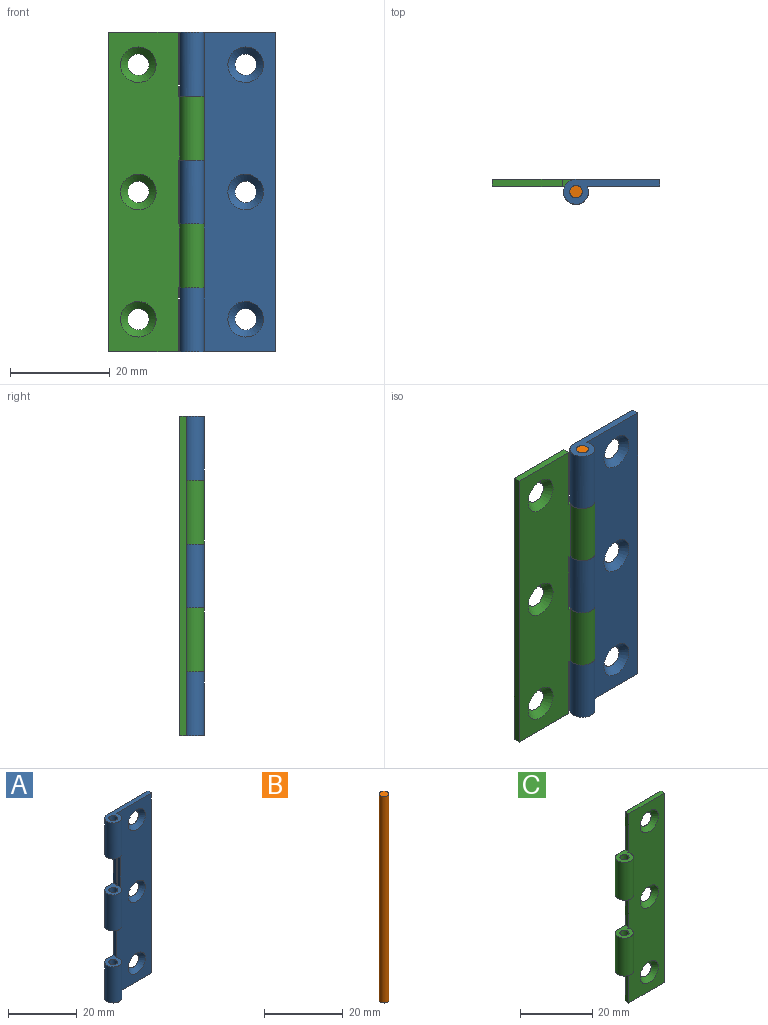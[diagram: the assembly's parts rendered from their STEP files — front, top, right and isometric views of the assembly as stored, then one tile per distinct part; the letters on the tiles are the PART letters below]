
ASSEMBLY  parts=3 mates=2
PART A: 20 faces, bbox 19.2x5x64 mm
  f0: cylinder r=2.5mm len=38.4mm, axis (0,0,-1), area 343.6mm2, adj f2,f5,f7,f12,f15,f16,f17
  f1: cylinder r=2.5mm len=12.8mm, axis (0,0,-1), area 165.4mm2, adj f2,f5,f8,f13
  f2: plane 64x14.5mm, normal (0,-1,0), area 803.3mm2, adj f0,f1,f6,f7,f8,f9,f10,f11
  f3: cylinder r=1.25mm len=12.8mm, axis (0,0,-1), area 100.5mm2, adj f7,f15
  f4: cylinder r=1.25mm len=12.8mm, axis (0,0,-1), area 100.5mm2, adj f8,f13
  f5: plane 64x16.75mm, normal (0,1,0), area 964.8mm2, adj f0,f1,f6,f7,f8,f9,f10,f11
  f6: plane 64x1.4mm, normal (1,0,0), area 89.6mm2, adj f2,f5,f7,f8
  f7: plane 19.25x5mm, normal (0,0,1), area 35.9mm2, adj f0,f2,f3,f5,f6
  f8: plane 19.25x5mm, normal (0,0,-1), area 35.9mm2, adj f1,f2,f4,f5,f6
  f9: cone r=2.15mm half-angle=45deg, axis (0,-1,0), area 35.5mm2, adj f2,f5
  f10: cone r=2.15mm half-angle=45deg, axis (0,-1,0), area 35.5mm2, adj f2,f5
  f11: cone r=2.15mm half-angle=45deg, axis (0,-1,0), area 35.5mm2, adj f2,f5
  f12: plane 5x5mm, normal (0,0,-1), area 16mm2, adj f0,f2,f5,f14,f19
  f13: plane 5x5mm, normal (0,0,1), area 16mm2, adj f1,f2,f4,f5,f14
  f14: plane 12.8x1.4mm, normal (-1,0,0), area 17.9mm2, adj f2,f5,f12,f13
  f15: plane 5x4.95mm, normal (0,0,-1), area 15.9mm2, adj f0,f2,f3,f5,f17,f18
  f16: plane 5x4.95mm, normal (0,0,1), area 15.9mm2, adj f0,f2,f5,f17,f18,f19
  f17: plane 12.8x1mm, normal (-1,0,0), area 12.8mm2, adj f0,f15,f16
  f18: plane 12.8x1.4mm, normal (-1,0,0), area 17.9mm2, adj f2,f5,f15,f16
  f19: cylinder r=1.25mm len=12.8mm, axis (0,0,-1), area 100.5mm2, adj f12,f16
PART B: 3 faces, bbox 2.5x2.5x64 mm
  f0: cylinder r=1.25mm len=64mm, axis (0,0,-1), area 502.7mm2, adj f1,f2
  f1: plane 2.5x2.5mm, normal (0,0,1), area 4.9mm2, adj f0
  f2: plane 2.5x2.5mm, normal (0,0,-1), area 4.9mm2, adj f0
PART C: 19 faces, bbox 19.2x5x64 mm
  f0: cylinder r=2.5mm len=12.8mm, axis (0,0,-1), area 165.4mm2, adj f2,f3,f14,f15
  f1: cylinder r=2.5mm len=12.8mm, axis (0,0,-1), area 165.4mm2, adj f2,f3,f10,f12
  f2: plane 64x14.5mm, normal (0,-1,0), area 789.7mm2, adj f0,f1,f4,f5,f6,f7,f8,f9
  f3: plane 64x16.75mm, normal (0,1,0), area 922.4mm2, adj f0,f1,f4,f5,f6,f7,f8,f9
  f4: plane 13.99x1.4mm, normal (0,0,1), area 19.6mm2, adj f2,f3,f6,f16
  f5: plane 13.99x1.4mm, normal (0,0,-1), area 19.6mm2, adj f2,f3,f6,f11
  f6: plane 64x1.4mm, normal (1,0,0), area 89.6mm2, adj f2,f3,f4,f5
  f7: cone r=2.15mm half-angle=45deg, axis (0,-1,0), area 35.5mm2, adj f2,f3
  f8: cone r=2.15mm half-angle=45deg, axis (0,-1,0), area 35.5mm2, adj f2,f3
  f9: cone r=2.15mm half-angle=45deg, axis (0,-1,0), area 35.5mm2, adj f2,f3
  f10: plane 5.25x5mm, normal (0,0,-1), area 16.3mm2, adj f1,f2,f3,f11,f17
  f11: plane 12.8x1.4mm, normal (-1,0,0), area 17.9mm2, adj f2,f3,f5,f10
  f12: plane 5.25x5mm, normal (0,0,1), area 16.3mm2, adj f1,f2,f3,f13,f17
  f13: plane 12.8x1.4mm, normal (-1,0,0), area 17.9mm2, adj f2,f3,f12,f14
  f14: plane 5.25x5mm, normal (0,0,-1), area 16.3mm2, adj f0,f2,f3,f13,f18
  f15: plane 5.25x5mm, normal (0,0,1), area 16.3mm2, adj f0,f2,f3,f16,f18
  f16: plane 12.8x1.4mm, normal (-1,0,0), area 17.9mm2, adj f2,f3,f4,f15
  f17: cylinder r=1.25mm len=12.8mm, axis (0,0,-1), area 100.5mm2, adj f10,f12
  f18: cylinder r=1.25mm len=12.8mm, axis (0,0,-1), area 100.5mm2, adj f14,f15
PLACE A rot(axis=(0,0,1),0deg) t=(0,0,0)mm
PLACE B at identity
PLACE C rot(axis=(0,-1,0),180deg) t=(0,0,64)mm
MATE revolute A.f0 <-> B.f0  axis (0,0,-1) through (0,0,64)mm
MATE revolute B.f0 <-> C.f0  axis (0,0,-1) through (0,0,64)mm
